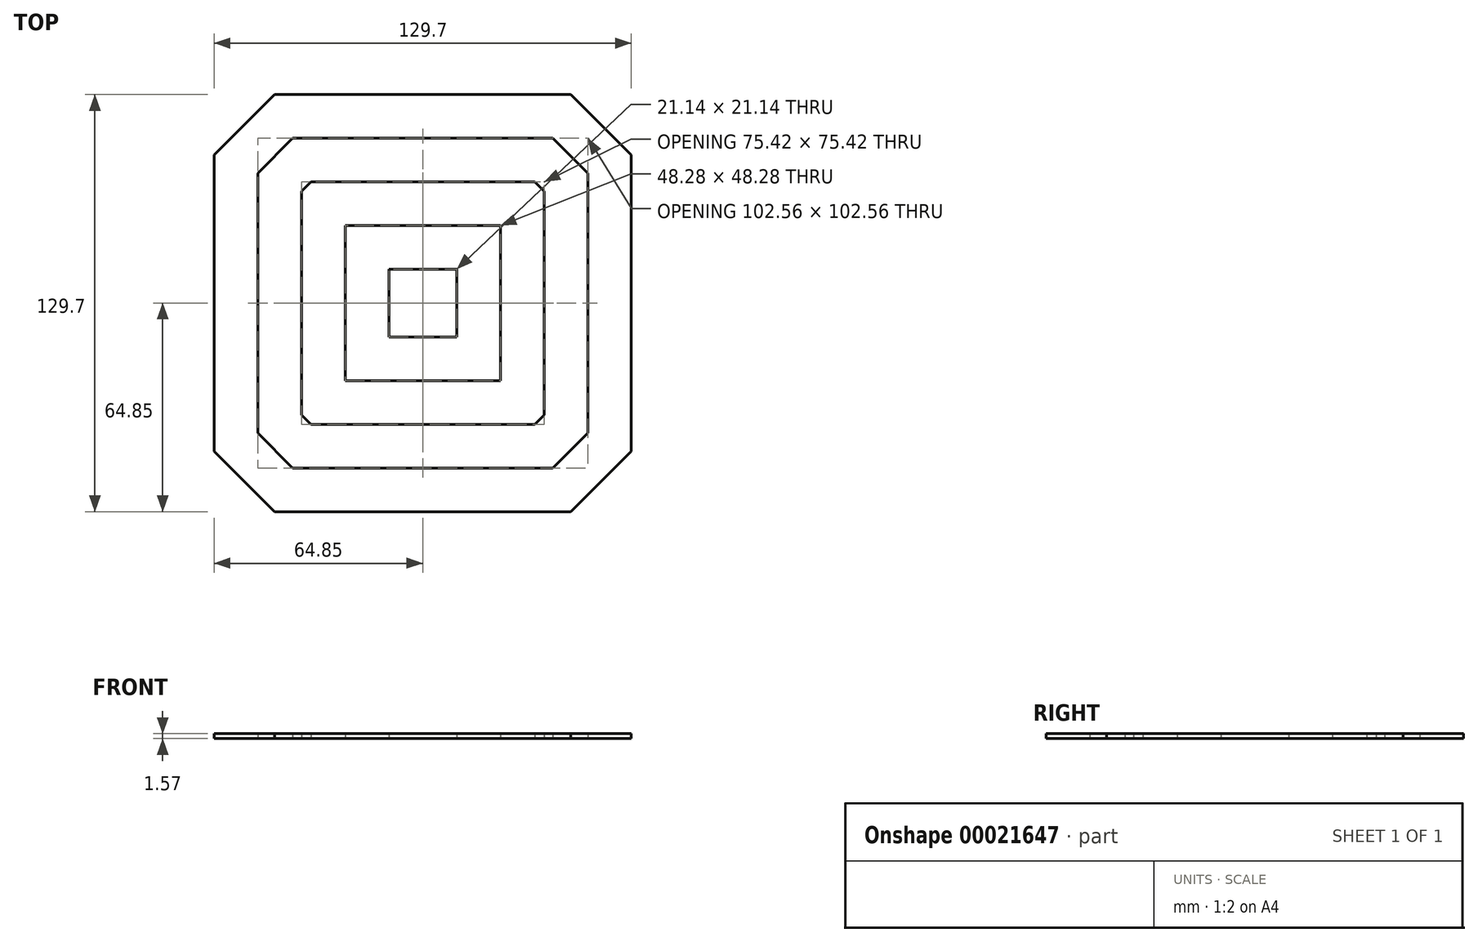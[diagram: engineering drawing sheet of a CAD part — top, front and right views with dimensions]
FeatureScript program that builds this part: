
annotation { "Feature Type Name" : "Feature", "Feature Type Description" : "" }
export const myFeature = defineFeature(function(context is Context, id is Id, definition is map)
    precondition{}
    {
        {
            var Q0;
            Q0=qCreatedBy(makeId("Top.planeOp"),FACE);
            var sketch = newSketch(context, id + "F0", { "sketchPlane" : qUnion([Q0])});
            skLineSegment(sketch, "E0.0", {"start": v(51.28, 40.43) * mm, "end": v(51.28, -40.43) * mm});
            skLineSegment(sketch, "E1.0", {"start": v(40.43, 51.28) * mm, "end": v(-40.43, 51.28) * mm});
            skLineSegment(sketch, "E2.0", {"start": v(-51.28, 40.43) * mm, "end": v(-51.28, -40.43) * mm});
            skLineSegment(sketch, "E3.0", {"start": v(40.43, -51.28) * mm, "end": v(-40.43, -51.28) * mm});
            skLineSegment(sketch, "E4.0", {"start": v(-51.28, 40.43) * mm, "end": v(-40.43, 51.28) * mm});
            skLineSegment(sketch, "E4.2", {"start": v(40.43, 51.28) * mm, "end": v(51.28, 40.43) * mm});
            skLineSegment(sketch, "E4.4", {"start": v(51.28, -40.43) * mm, "end": v(40.43, -51.28) * mm});
            skLineSegment(sketch, "E4.6", {"start": v(-40.43, -51.28) * mm, "end": v(-51.28, -40.43) * mm});
            skLineSegment(sketch, "E5.0", {"start": v(46.05, -64.85) * mm, "end": v(-46.05, -64.85) * mm});
            skLineSegment(sketch, "E5.1", {"start": v(64.85, -46.05) * mm, "end": v(46.05, -64.85) * mm});
            skLineSegment(sketch, "E5.2", {"start": v(64.85, 46.05) * mm, "end": v(64.85, -46.05) * mm});
            skLineSegment(sketch, "E5.3", {"start": v(46.05, 64.85) * mm, "end": v(64.85, 46.05) * mm});
            skLineSegment(sketch, "E5.4", {"start": v(46.05, 64.85) * mm, "end": v(-46.05, 64.85) * mm});
            skLineSegment(sketch, "E5.5", {"start": v(-46.05, -64.85) * mm, "end": v(-64.85, -46.05) * mm});
            skLineSegment(sketch, "E5.6", {"start": v(-64.85, 46.05) * mm, "end": v(-46.05, 64.85) * mm});
            skLineSegment(sketch, "E5.7", {"start": v(-64.85, 46.05) * mm, "end": v(-64.85, -46.05) * mm});
            skLineSegment(sketch, "E6.0", {"start": v(-37.7, 34.81) * mm, "end": v(-37.7, -34.81) * mm});
            skLineSegment(sketch, "E6.1", {"start": v(-34.81, -37.7) * mm, "end": v(-37.7, -34.81) * mm});
            skLineSegment(sketch, "E6.2", {"start": v(34.81, -37.7) * mm, "end": v(-34.81, -37.7) * mm});
            skLineSegment(sketch, "E6.3", {"start": v(37.7, -34.81) * mm, "end": v(34.81, -37.7) * mm});
            skLineSegment(sketch, "E6.4", {"start": v(37.7, 34.81) * mm, "end": v(37.7, -34.81) * mm});
            skLineSegment(sketch, "E6.5", {"start": v(-37.7, 34.81) * mm, "end": v(-34.81, 37.7) * mm});
            skLineSegment(sketch, "E6.6", {"start": v(34.81, 37.7) * mm, "end": v(37.7, 34.81) * mm});
            skLineSegment(sketch, "E6.7", {"start": v(34.81, 37.71) * mm, "end": v(-34.81, 37.71) * mm});
            skLineSegment(sketch, "E7.0", {"start": v(24.14, 24.14) * mm, "end": v(-24.14, 24.14) * mm});
            skLineSegment(sketch, "E7.1", {"start": v(24.14, 24.14) * mm, "end": v(24.14, -24.14) * mm});
            skLineSegment(sketch, "E7.2", {"start": v(24.14, -24.14) * mm, "end": v(-24.14, -24.14) * mm});
            skLineSegment(sketch, "E7.3", {"start": v(-24.14, 24.14) * mm, "end": v(-24.14, -24.14) * mm});
            skLineSegment(sketch, "E8.0", {"start": v(10.57, 10.57) * mm, "end": v(-10.57, 10.57) * mm});
            skLineSegment(sketch, "E8.1", {"start": v(10.57, 10.57) * mm, "end": v(10.57, -10.57) * mm});
            skLineSegment(sketch, "E8.2", {"start": v(10.57, -10.57) * mm, "end": v(-10.57, -10.57) * mm});
            skLineSegment(sketch, "E8.3", {"start": v(-10.57, 10.57) * mm, "end": v(-10.57, -10.57) * mm});
            skPoint(sketch, "E9", {"position": v(10.57, 0) * mm});
            skPoint(sketch, "E10", {"position": v(0, 10.57) * mm});
            skLineSegment(sketch, "E11", {"start": v(10.57, 0) * mm, "end": v(24.14, 0) * mm, "construction": true});
            skLineSegment(sketch, "E12", {"start": v(24.14, 0) * mm, "end": v(37.7, 0) * mm, "construction": true});
            skLineSegment(sketch, "E13", {"start": v(37.7, 0) * mm, "end": v(51.28, 0) * mm, "construction": true});
            skLineSegment(sketch, "E14", {"start": v(51.28, 0) * mm, "end": v(64.85, 0) * mm, "construction": true});
            skPoint(sketch, "E15", {"position": v(45.86, 45.86) * mm});
            skPoint(sketch, "E16", {"position": v(-45.86, -45.86) * mm});
            skLineSegment(sketch, "E17", {"start": v(-45.86, -45.86) * mm, "end": v(45.86, 45.86) * mm, "construction": true});
            skLineSegment(sketch, "E18", {"start": v(-46.05, -64.85) * mm, "end": v(-46.05, 64.85) * mm, "construction": true});
            skLineSegment(sketch, "E19", {"start": v(-88.5, 0) * mm, "end": v(80.5, 0) * mm, "construction": true});
            skSolve(sketch);
        }
        {
            var Q0;
            {var subQ24=sQuery(id+"F0.wireOp",EDGE,"E0.0");Q0=makeQuery(id+"F0.imprint","IMPRINT",FACE,{"disambiguationData":[TD([[makeQuery(id+"F0.imprint","IMPRINT",EDGE,{"derivedFrom":subQ24}),1.0]])]});}
            var sketch = newSketch(context, id + "F1", { "sketchPlane" : qUnion([Q0])});
            skCircle(sketch, "E20", {"center": v(0, 0) * mm, "radius": 0.79 * mm});
            skCircle(sketch, "E21.1.0.0", {"center": v(13.57, 0) * mm, "radius": 0.79 * mm});
            skCircle(sketch, "E21.2.0.0", {"center": v(27.14, 0) * mm, "radius": 0.79 * mm});
            skCircle(sketch, "E21.3.0.0", {"center": v(40.7, 0) * mm, "radius": 0.79 * mm});
            skCircle(sketch, "E21.4.0.0", {"center": v(54.28, 0) * mm, "radius": 0.79 * mm});
            skCircle(sketch, "E21.5.0.0", {"center": v(67.85, 0) * mm, "radius": 0.79 * mm});
            skLineSegment(sketch, "E21.direction1", {"start": v(0, 0) * mm, "end": v(13.57, 0) * mm, "construction": true});
            skLineSegment(sketch, "E22.1.5", {"start": v(0, 0) * mm, "end": v(9.6, 9.6) * mm, "construction": true});
            skCircle(sketch, "E22.1.8", {"center": v(38.38, 38.38) * mm, "radius": 0.79 * mm});
            skCircle(sketch, "E22.1.9", {"center": v(47.98, 47.98) * mm, "radius": 0.79 * mm});
            skCircle(sketch, "E22.1.10", {"center": v(19.2, 19.2) * mm, "radius": 0.79 * mm});
            skCircle(sketch, "E22.1.11", {"center": v(9.6, 9.6) * mm, "radius": 0.79 * mm});
            skCircle(sketch, "E22.1.13", {"center": v(28.79, 28.79) * mm, "radius": 0.79 * mm});
            skLineSegment(sketch, "E22.2.5", {"start": v(0, 0) * mm, "end": v(0, 13.57) * mm, "construction": true});
            skCircle(sketch, "E22.2.8", {"center": v(0, 54.28) * mm, "radius": 0.79 * mm});
            skCircle(sketch, "E22.2.9", {"center": v(0, 67.85) * mm, "radius": 0.79 * mm});
            skCircle(sketch, "E22.2.10", {"center": v(0, 27.14) * mm, "radius": 0.79 * mm});
            skCircle(sketch, "E22.2.11", {"center": v(0, 13.57) * mm, "radius": 0.79 * mm});
            skCircle(sketch, "E22.2.13", {"center": v(0, 40.7) * mm, "radius": 0.79 * mm});
            skLineSegment(sketch, "E22.3.5", {"start": v(0, 0) * mm, "end": v(-9.6, 9.6) * mm, "construction": true});
            skCircle(sketch, "E22.3.8", {"center": v(-38.38, 38.38) * mm, "radius": 0.79 * mm});
            skCircle(sketch, "E22.3.9", {"center": v(-47.98, 47.98) * mm, "radius": 0.79 * mm});
            skCircle(sketch, "E22.3.10", {"center": v(-19.2, 19.2) * mm, "radius": 0.79 * mm});
            skCircle(sketch, "E22.3.11", {"center": v(-9.6, 9.6) * mm, "radius": 0.79 * mm});
            skCircle(sketch, "E22.3.13", {"center": v(-28.79, 28.79) * mm, "radius": 0.79 * mm});
            skLineSegment(sketch, "E22.4.5", {"start": v(0, 0) * mm, "end": v(-13.57, 0) * mm, "construction": true});
            skCircle(sketch, "E22.4.8", {"center": v(-54.28, 0) * mm, "radius": 0.79 * mm});
            skCircle(sketch, "E22.4.9", {"center": v(-67.85, 0) * mm, "radius": 0.79 * mm});
            skCircle(sketch, "E22.4.10", {"center": v(-27.14, 0) * mm, "radius": 0.79 * mm});
            skCircle(sketch, "E22.4.11", {"center": v(-13.57, 0) * mm, "radius": 0.79 * mm});
            skCircle(sketch, "E22.4.13", {"center": v(-40.7, 0) * mm, "radius": 0.79 * mm});
            skLineSegment(sketch, "E22.5.5", {"start": v(0, 0) * mm, "end": v(-9.6, -9.6) * mm, "construction": true});
            skCircle(sketch, "E22.5.8", {"center": v(-38.38, -38.38) * mm, "radius": 0.79 * mm});
            skCircle(sketch, "E22.5.9", {"center": v(-47.98, -47.98) * mm, "radius": 0.79 * mm});
            skCircle(sketch, "E22.5.10", {"center": v(-19.2, -19.2) * mm, "radius": 0.79 * mm});
            skCircle(sketch, "E22.5.11", {"center": v(-9.6, -9.6) * mm, "radius": 0.79 * mm});
            skCircle(sketch, "E22.5.13", {"center": v(-28.79, -28.79) * mm, "radius": 0.79 * mm});
            skLineSegment(sketch, "E22.6.5", {"start": v(0, 0) * mm, "end": v(0, -13.57) * mm, "construction": true});
            skCircle(sketch, "E22.6.8", {"center": v(0, -54.28) * mm, "radius": 0.79 * mm});
            skCircle(sketch, "E22.6.9", {"center": v(0, -67.85) * mm, "radius": 0.79 * mm});
            skCircle(sketch, "E22.6.10", {"center": v(0, -27.14) * mm, "radius": 0.79 * mm});
            skCircle(sketch, "E22.6.11", {"center": v(0, -13.57) * mm, "radius": 0.79 * mm});
            skCircle(sketch, "E22.6.13", {"center": v(0, -40.7) * mm, "radius": 0.79 * mm});
            skLineSegment(sketch, "E22.7.5", {"start": v(0, 0) * mm, "end": v(9.6, -9.6) * mm, "construction": true});
            skCircle(sketch, "E22.7.8", {"center": v(38.38, -38.38) * mm, "radius": 0.79 * mm});
            skCircle(sketch, "E22.7.9", {"center": v(47.98, -47.98) * mm, "radius": 0.79 * mm});
            skCircle(sketch, "E22.7.10", {"center": v(19.2, -19.2) * mm, "radius": 0.79 * mm});
            skCircle(sketch, "E22.7.11", {"center": v(9.6, -9.6) * mm, "radius": 0.79 * mm});
            skCircle(sketch, "E22.7.13", {"center": v(28.79, -28.79) * mm, "radius": 0.79 * mm});
            skSolve(sketch);
        }
        {
            var Q0;
            Q0=makeQuery(id+"F0.imprint","IMPRINT",FACE,{"disambiguationData":[TD([[makeQuery(id+"F0.imprint","IMPRINT",EDGE,{"derivedFrom":sQuery(id+"F0.wireOp",EDGE,"E0.0")}),1.0]])]});
            extrude(context, id + "F2", {"entities" : qUnion([Q0]), "depth" : 1.57 * mm});
        }
        {
            var Q0;
            Q0=makeQuery(id+"F0.imprint","IMPRINT",FACE,{"disambiguationData":[TD([[makeQuery(id+"F0.imprint","IMPRINT",EDGE,{"derivedFrom":sQuery(id+"F0.wireOp",EDGE,"E0.0")}),-1.0]])]});
            extrude(context, id + "F3", {"entities" : qUnion([Q0]), "depth" : 1.57 * mm});
        }
        {
            var Q0;
            Q0=makeQuery(id+"F0.imprint","IMPRINT",FACE,{"disambiguationData":[TD([[makeQuery(id+"F0.imprint","IMPRINT",EDGE,{"derivedFrom":sQuery(id+"F0.wireOp",EDGE,"E6.0")}),1.0]])]});
            extrude(context, id + "F4", {"entities" : qUnion([Q0]), "depth" : 1.57 * mm});
        }
        {
            var Q0;
            Q0=makeQuery(id+"F0.imprint","IMPRINT",FACE,{"disambiguationData":[TD([[makeQuery(id+"F0.imprint","IMPRINT",EDGE,{"derivedFrom":sQuery(id+"F0.wireOp",EDGE,"E7.0")}),1.0]])]});
            extrude(context, id + "F5", {"entities" : qUnion([Q0]), "depth" : 1.57 * mm});
        }
        {
            var Q0;
            Q0=makeQuery(id+"F0.imprint","IMPRINT",FACE,{"disambiguationData":[TD([[makeQuery(id+"F0.imprint","IMPRINT",EDGE,{"derivedFrom":sQuery(id+"F0.wireOp",EDGE,"E8.0")}),1.0]])]});
            extrude(context, id + "F6", {"entities" : qUnion([Q0]), "depth" : 1.57 * mm});
        }
    });
